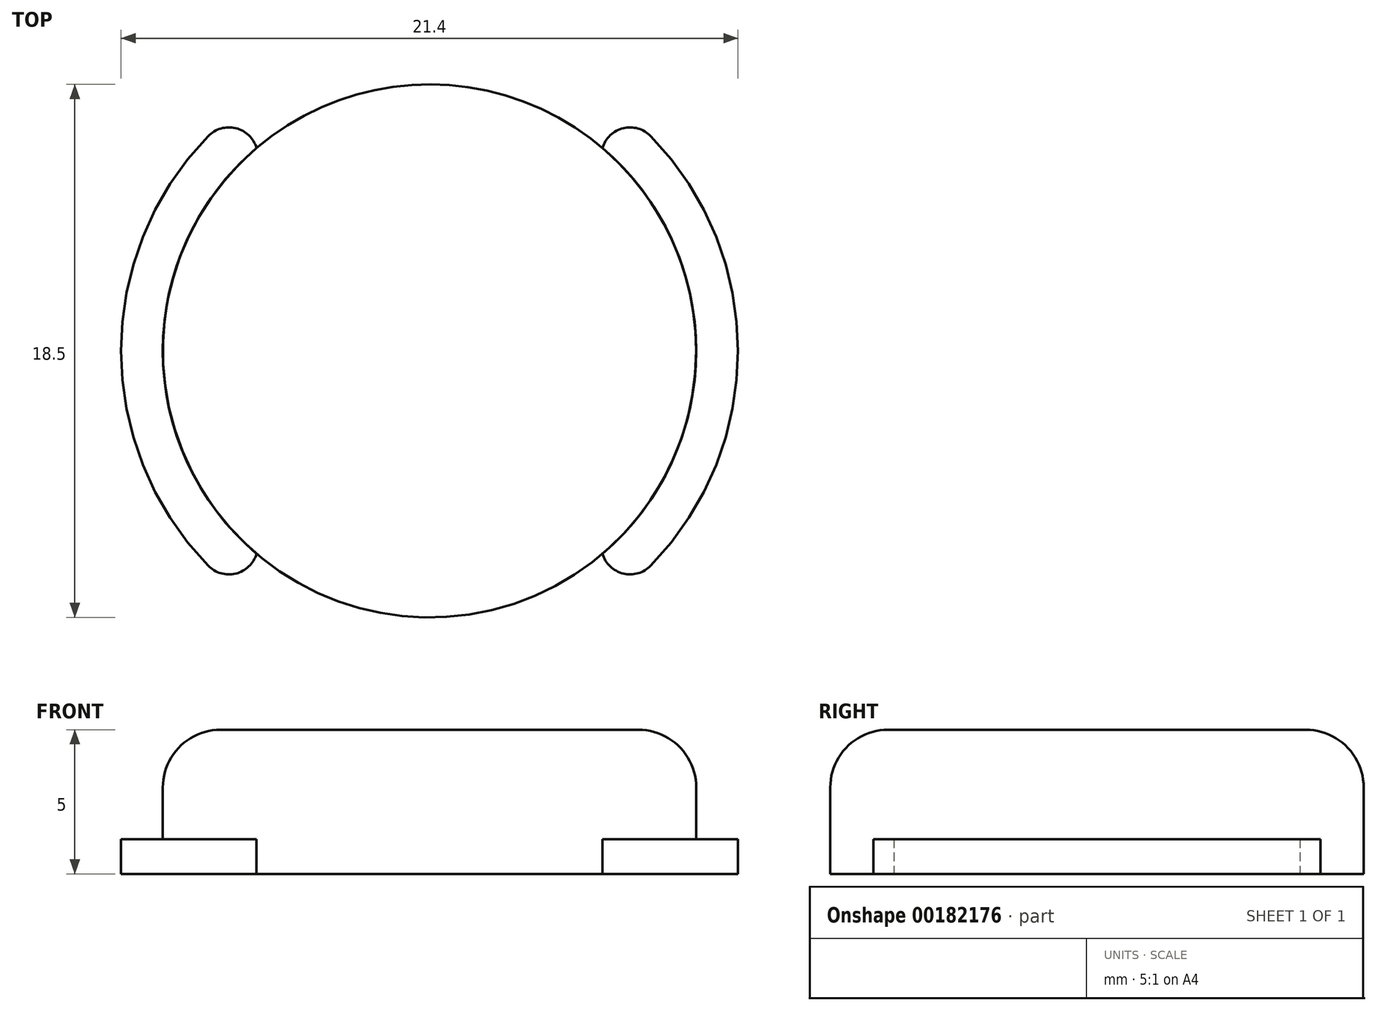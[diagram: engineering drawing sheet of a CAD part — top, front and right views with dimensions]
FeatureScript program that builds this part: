
annotation { "Feature Type Name" : "Feature", "Feature Type Description" : "" }
export const myFeature = defineFeature(function(context is Context, id is Id, definition is map)
    precondition{}
    {
        {
            var Q0;
            Q0=qCreatedBy(makeId("Top.planeOp"),FACE);
            var sketch = newSketch(context, id + "F0", { "sketchPlane" : qUnion([Q0])});
            skCircle(sketch, "E0", {"center": v(0, 0) * mm, "radius": 9.25 * mm});
            skSolve(sketch);
        }
        {
            var Q0;
            Q0 = qSketchRegion(id + "F0", true);
            extrude(context, id + "F1", {"entities" : qUnion([Q0]), "depth" : 5 * mm});
        }
        {
            var Q0;
            Q0=makeQuery(id+"F1.opExtrude","CAP_FACE",FACE,{"disambiguationData":[OSD([sQuery(id+"F0.wireOp",EDGE,"E0")])],"isStart":true});
            var sketch = newSketch(context, id + "F2", { "sketchPlane" : qUnion([Q0])});
            skCircle(sketch, "E1", {"center": v(0, 0) * mm, "radius": 10.7 * mm});
            skLineSegment(sketch, "E2.bottom", {"start": v(-6, 15.08) * mm, "end": v(6, 15.08) * mm});
            skLineSegment(sketch, "E2.top", {"start": v(-6, -15.08) * mm, "end": v(6, -15.08) * mm});
            skLineSegment(sketch, "E2.left", {"start": v(-6, 15.08) * mm, "end": v(-6, -15.08) * mm});
            skLineSegment(sketch, "E2.right", {"start": v(6, 15.08) * mm, "end": v(6, -15.08) * mm});
            skSolve(sketch);
        }
        {
            var Q0;
            {var subQ0=sQuery(id+"F2.wireOp",EDGE,"E2.left");var subQ1=sQuery(id+"F2.wireOp",EDGE,"E1");var subQ2=makeQuery(id+"F2.imprint","INTERSECT",VERTEX,{"disambiguationData":[OD(0.0)],"derivedFrom":[subQ1,subQ0]});Q0=makeQuery(id+"F2.imprint","IMPRINT",FACE,{"disambiguationData":[TD([[makeQuery(id+"F2.imprint","IMPRINT",EDGE,{"disambiguationData":[TD([[subQ2,-1.0]])],"derivedFrom":subQ1}),1.0]])]});}
            var Q1;
            {var subQ0=sQuery(id+"F2.wireOp",EDGE,"E2.left");var subQ1=makeQuery(id+"F1.opExtrude","CAP_EDGE",EDGE,{"disambiguationData":[OSD([sQuery(id+"F0.wireOp",EDGE,"E0")])],"isStart":true});var subQ2=makeQuery(id+"F2.imprint","INTERSECT",VERTEX,{"disambiguationData":[OD(0.0)],"derivedFrom":[subQ1,subQ0]});Q1=makeQuery(id+"F2.imprint","IMPRINT",FACE,{"disambiguationData":[TD([[makeQuery(id+"F2.imprint","IMPRINT",EDGE,{"disambiguationData":[TD([[subQ2,-1.0]])],"derivedFrom":subQ0}),-1.0]])]});}
            var Q2;
            {var subQ0=sQuery(id+"F2.wireOp",EDGE,"E2.left");var subQ1=makeQuery(id+"F1.opExtrude","CAP_EDGE",EDGE,{"disambiguationData":[OSD([sQuery(id+"F0.wireOp",EDGE,"E0")])],"isStart":true});var subQ2=makeQuery(id+"F2.imprint","INTERSECT",VERTEX,{"disambiguationData":[OD(0.0)],"derivedFrom":[subQ1,subQ0]});Q2=makeQuery(id+"F2.imprint","IMPRINT",FACE,{"disambiguationData":[TD([[makeQuery(id+"F2.imprint","IMPRINT",EDGE,{"disambiguationData":[TD([[subQ2,-1.0]])],"derivedFrom":subQ0}),1.0]])]});}
            var Q3;
            {var subQ0=sQuery(id+"F2.wireOp",EDGE,"E2.right");var subQ1=makeQuery(id+"F1.opExtrude","CAP_EDGE",EDGE,{"disambiguationData":[OSD([sQuery(id+"F0.wireOp",EDGE,"E0")])],"isStart":true});var subQ2=makeQuery(id+"F2.imprint","INTERSECT",VERTEX,{"disambiguationData":[OD(0.0)],"derivedFrom":[subQ1,subQ0]});Q3=makeQuery(id+"F2.imprint","IMPRINT",FACE,{"disambiguationData":[TD([[makeQuery(id+"F2.imprint","IMPRINT",EDGE,{"disambiguationData":[TD([[subQ2,-1.0]])],"derivedFrom":subQ0}),1.0]])]});}
            var Q4;
            {var subQ0=sQuery(id+"F2.wireOp",EDGE,"E2.right");var subQ1=sQuery(id+"F2.wireOp",EDGE,"E1");var subQ2=makeQuery(id+"F2.imprint","INTERSECT",VERTEX,{"disambiguationData":[OD(0.0)],"derivedFrom":[subQ1,subQ0]});Q4=makeQuery(id+"F2.imprint","IMPRINT",FACE,{"disambiguationData":[TD([[makeQuery(id+"F2.imprint","IMPRINT",EDGE,{"disambiguationData":[TD([[subQ2,1.0]])],"derivedFrom":subQ1}),1.0]])]});}
            extrude(context, id + "F3", {"entities" : qUnion([Q0, Q1, Q2, Q3, Q4]), "operationType" : NewBodyOperationType.ADD, "oppositeDirection" : true, "depth" : 1.2 * mm});
        }
        {
            var Q0;
            {var subQ0=sQuery(id+"F2.wireOp",EDGE,"E2.right");var subQ1=sQuery(id+"F2.wireOp",EDGE,"E1");Q0=makeQuery(id+"F3.opExtrude","SWEPT_EDGE",EDGE,{"disambiguationData":[OSD([subQ1,subQ0]),TDD([makeQuery(id+"F2.imprint","INTERSECT",VERTEX,{"disambiguationData":[OD(0.0)],"derivedFrom":[subQ1,subQ0]})])]});}
            var Q1;
            {var subQ0=sQuery(id+"F2.wireOp",EDGE,"E2.left");var subQ1=sQuery(id+"F2.wireOp",EDGE,"E1");Q1=makeQuery(id+"F3.opExtrude","SWEPT_EDGE",EDGE,{"disambiguationData":[OSD([subQ1,subQ0]),TDD([makeQuery(id+"F2.imprint","INTERSECT",VERTEX,{"disambiguationData":[OD(0.0)],"derivedFrom":[subQ1,subQ0]})])]});}
            var Q2;
            {var subQ0=sQuery(id+"F2.wireOp",EDGE,"E2.right");var subQ1=sQuery(id+"F2.wireOp",EDGE,"E1");Q2=makeQuery(id+"F3.opExtrude","SWEPT_EDGE",EDGE,{"disambiguationData":[OSD([subQ1,subQ0]),TDD([makeQuery(id+"F2.imprint","INTERSECT",VERTEX,{"disambiguationData":[OD(1.0)],"derivedFrom":[subQ1,subQ0]})])]});}
            var Q3;
            {var subQ0=sQuery(id+"F2.wireOp",EDGE,"E2.left");var subQ1=sQuery(id+"F2.wireOp",EDGE,"E1");Q3=makeQuery(id+"F3.opExtrude","SWEPT_EDGE",EDGE,{"disambiguationData":[OSD([subQ1,subQ0]),TDD([makeQuery(id+"F2.imprint","INTERSECT",VERTEX,{"disambiguationData":[OD(1.0)],"derivedFrom":[subQ1,subQ0]})])]});}
            fillet(context, id + "F4", {"entities" : qUnion([Q0, Q1, Q2, Q3]), "radius" : 1 * mm, "tangentPropagation" : true, "allowEdgeOverflow" : false});
        }
        {
            var Q0;
            Q0=makeQuery(id+"F1.opExtrude","CAP_EDGE",EDGE,{"disambiguationData":[OSD([sQuery(id+"F0.wireOp",EDGE,"E0")])],"isStart":false});
            fillet(context, id + "F5", {"entities" : qUnion([Q0]), "radius" : 2 * mm, "tangentPropagation" : true, "allowEdgeOverflow" : false});
        }
    });
